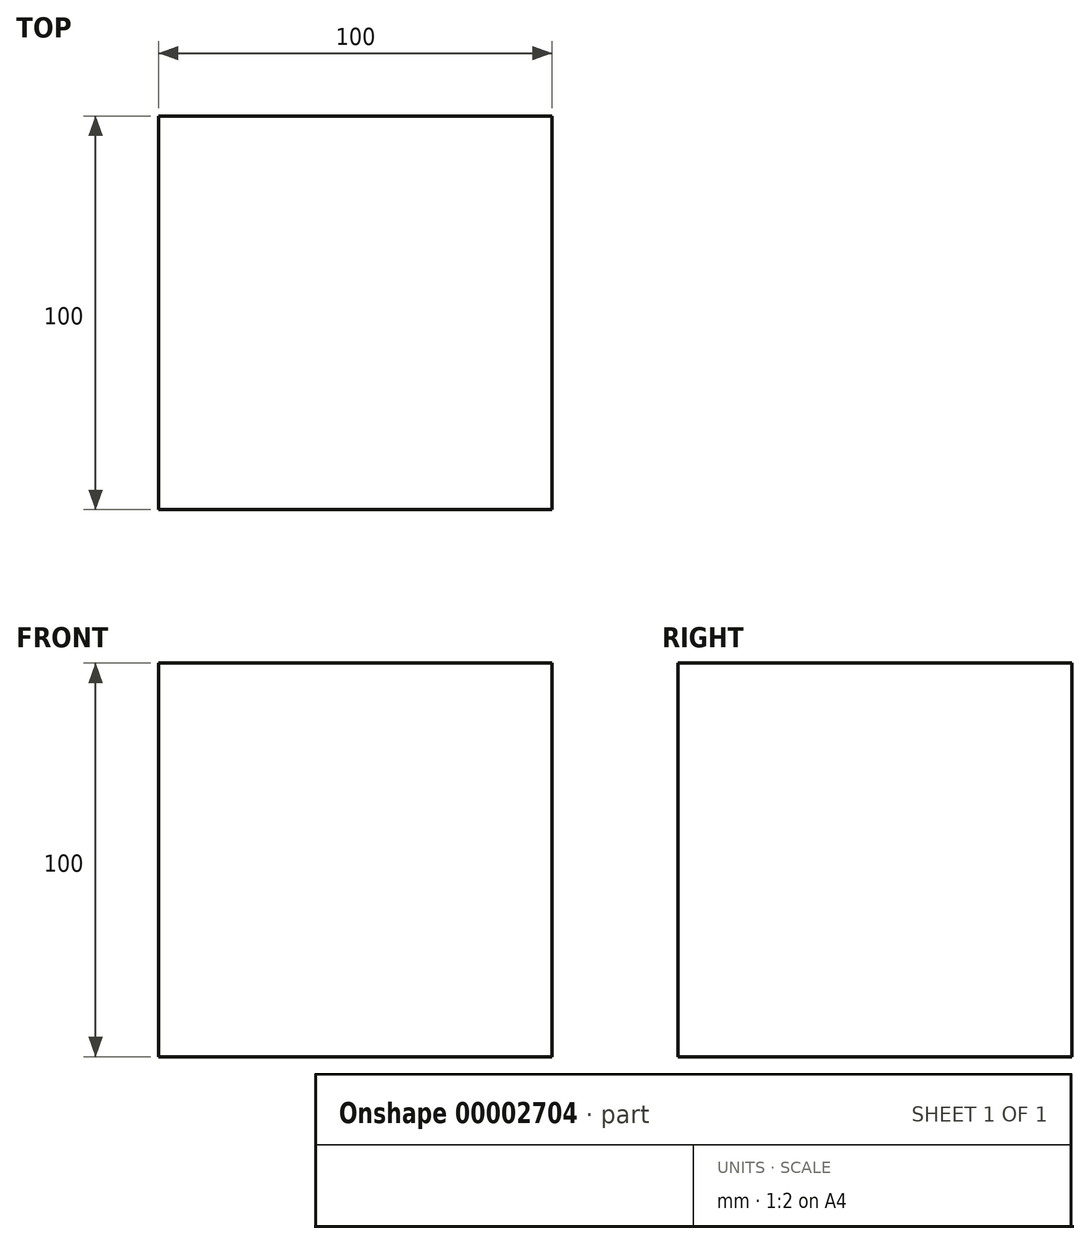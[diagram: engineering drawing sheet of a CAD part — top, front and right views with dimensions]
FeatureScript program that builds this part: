
annotation { "Feature Type Name" : "Feature", "Feature Type Description" : "" }
export const myFeature = defineFeature(function(context is Context, id is Id, definition is map)
    precondition{}
    {
        {
            var Q0;
            Q0=qCreatedBy(makeId("Top.planeOp"),FACE);
            var sketch = newSketch(context, id + "F0", { "sketchPlane" : qUnion([Q0])});
            skLineSegment(sketch, "E0.bottom", {"start": v(0, 0) * mm, "end": v(100, 0) * mm});
            skLineSegment(sketch, "E0.top", {"start": v(0, 100) * mm, "end": v(100, 100) * mm});
            skLineSegment(sketch, "E0.left", {"start": v(0, 0) * mm, "end": v(0, 100) * mm});
            skLineSegment(sketch, "E0.right", {"start": v(100, 0) * mm, "end": v(100, 100) * mm});
            skSolve(sketch);
        }
        {
            var Q0;
            Q0 = qSketchRegion(id + "F0", true);
            extrude(context, id + "F1", {"entities" : qUnion([Q0]), "depth" : 100 * mm});
        }
    });
